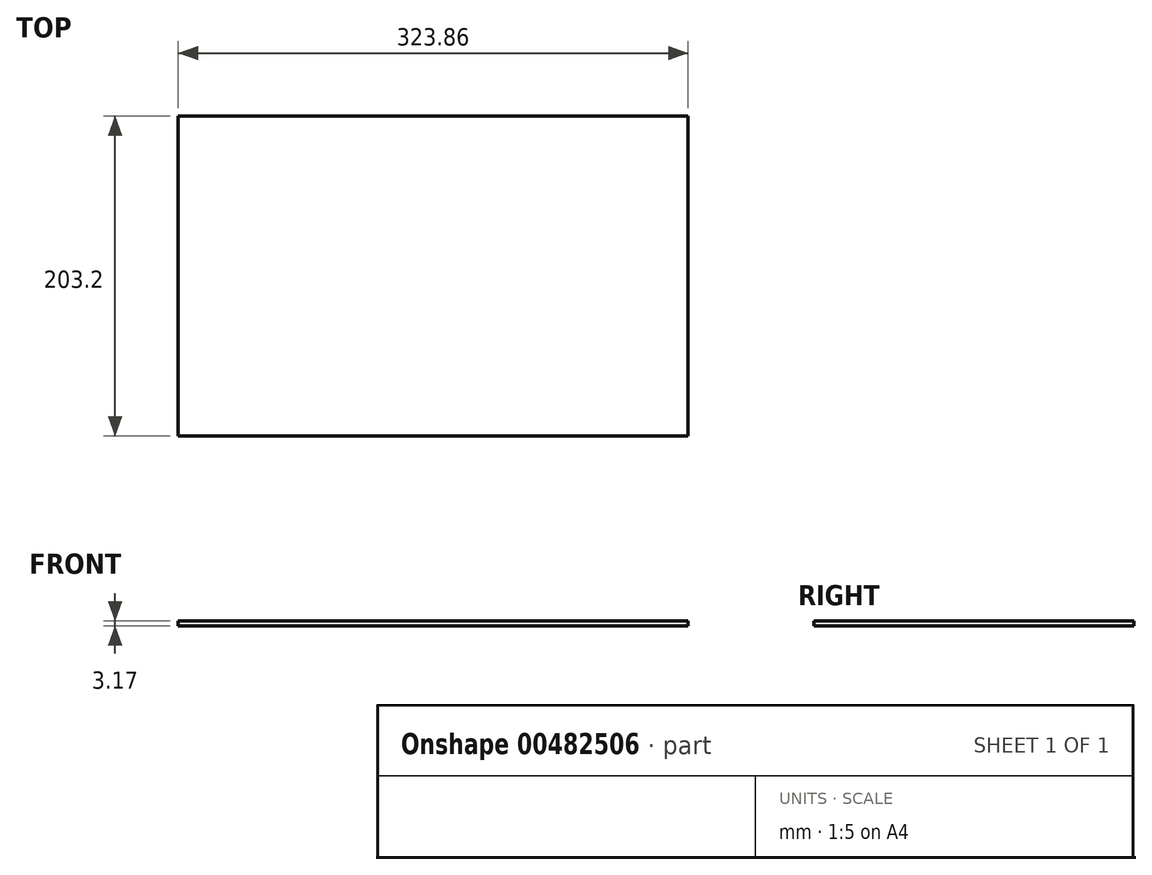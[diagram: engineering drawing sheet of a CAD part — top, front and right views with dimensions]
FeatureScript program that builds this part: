
annotation { "Feature Type Name" : "Feature", "Feature Type Description" : "" }
export const myFeature = defineFeature(function(context is Context, id is Id, definition is map)
    precondition{}
    {
        {
            var Q0;
            Q0=qCreatedBy(makeId("Top.planeOp"),FACE);
            var sketch = newSketch(context, id + "F0", { "sketchPlane" : qUnion([Q0])});
            skLineSegment(sketch, "E0.bottom", {"start": v(161.92, 101.6) * mm, "end": v(-161.93, 101.6) * mm});
            skLineSegment(sketch, "E0.top", {"start": v(161.93, -101.6) * mm, "end": v(-161.92, -101.6) * mm});
            skLineSegment(sketch, "E0.left", {"start": v(161.92, 101.6) * mm, "end": v(161.93, -101.6) * mm});
            skLineSegment(sketch, "E0.right", {"start": v(-161.93, 101.6) * mm, "end": v(-161.92, -101.6) * mm});
            skPoint(sketch, "E0.middle", {"position": v(0, 0) * mm});
            skSolve(sketch);
        }
        {
            var Q0;
            Q0 = qSketchRegion(id + "F0", true);
            extrude(context, id + "F1", {"entities" : qUnion([Q0]), "depth" : 3.17 * mm});
        }
    });
